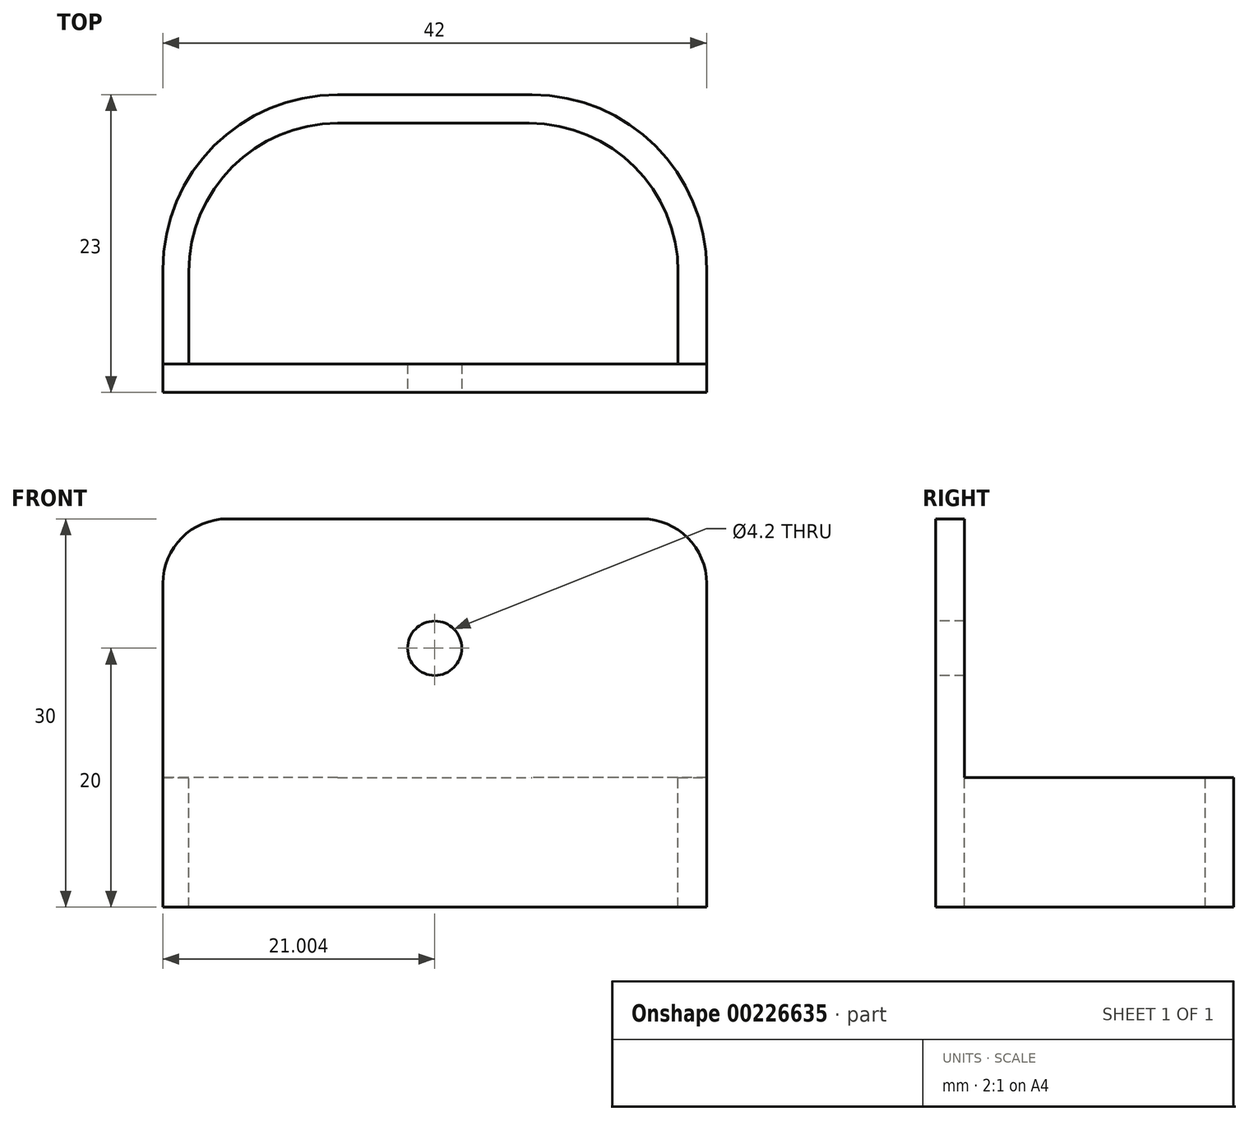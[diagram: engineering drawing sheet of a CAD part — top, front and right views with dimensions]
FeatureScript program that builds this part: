
annotation { "Feature Type Name" : "Feature", "Feature Type Description" : "" }
export const myFeature = defineFeature(function(context is Context, id is Id, definition is map)
    precondition{}
    {
        {
            var Q0;
            Q0=qCreatedBy(makeId("Top.planeOp"),FACE);
            var sketch = newSketch(context, id + "F0", { "sketchPlane" : qUnion([Q0])});
            skLineSegment(sketch, "E0.bottom", {"start": v(36.72, -41.29) * mm, "end": v(51.72, -41.29) * mm});
            skLineSegment(sketch, "E0.top", {"start": v(23.22, -64.29) * mm, "end": v(65.22, -64.29) * mm});
            skLineSegment(sketch, "E0.left", {"start": v(23.22, -54.79) * mm, "end": v(23.22, -64.29) * mm});
            skLineSegment(sketch, "E0.right", {"start": v(65.22, -54.79) * mm, "end": v(65.22, -64.29) * mm});
            skArc(sketch, "E1.filletArc", {"start": v(36.72, -41.29) * mm, "mid": v(27.18, -45.24) * mm, "end": v(23.22, -54.79) * mm});
            skArc(sketch, "E2.filletArc", {"start": v(65.22, -54.79) * mm, "mid": v(61.27, -45.24) * mm, "end": v(51.72, -41.29) * mm});
            skSolve(sketch);
        }
        {
            var Q0;
            Q0=makeQuery(id+"F0.imprint","IMPRINT",FACE,{"disambiguationData":[TD([[makeQuery(id+"F0.imprint","IMPRINT",EDGE,{"derivedFrom":sQuery(id+"F0.wireOp",EDGE,"E0.bottom")}),-1.0]])]});
            extrude(context, id + "F1", {"entities" : qUnion([Q0]), "depth" : 10 * mm});
        }
        {
            var Q0;
            Q0=makeQuery(id+"F1.opExtrude","CAP_FACE",FACE,{"disambiguationData":[OSD([sQuery(id+"F0.wireOp",EDGE,"E0.bottom"),sQuery(id+"F0.wireOp",EDGE,"E0.top"),sQuery(id+"F0.wireOp",EDGE,"E0.left"),sQuery(id+"F0.wireOp",EDGE,"E0.right"),sQuery(id+"F0.wireOp",EDGE,"E1.filletArc"),sQuery(id+"F0.wireOp",EDGE,"E2.filletArc")])],"isStart":false});
            var sketch = newSketch(context, id + "F2", { "sketchPlane" : qUnion([Q0])});
            skLineSegment(sketch, "E3.bottom", {"start": v(36.72, -43.49) * mm, "end": v(51.52, -43.49) * mm});
            skLineSegment(sketch, "E3.top", {"start": v(25.22, -62.09) * mm, "end": v(63.02, -62.09) * mm});
            skLineSegment(sketch, "E3.left", {"start": v(25.22, -54.99) * mm, "end": v(25.22, -62.09) * mm});
            skLineSegment(sketch, "E3.right", {"start": v(63.02, -54.99) * mm, "end": v(63.02, -62.09) * mm});
            skPoint(sketch, "E4.visualSharp", {"position": v(63.02, -43.49) * mm});
            skArc(sketch, "E4.filletArc", {"start": v(63.02, -54.99) * mm, "mid": v(59.66, -46.86) * mm, "end": v(51.52, -43.49) * mm});
            skPoint(sketch, "E5.visualSharp", {"position": v(25.22, -43.49) * mm});
            skArc(sketch, "E5.filletArc", {"start": v(36.72, -43.49) * mm, "mid": v(28.6, -46.86) * mm, "end": v(25.22, -54.99) * mm});
            skSolve(sketch);
        }
        {
            var Q0;
            Q0=qSketchRegion(id+"F2",true);
            extrude(context, id + "F3", {"entities" : qUnion([Q0]), "operationType" : NewBodyOperationType.REMOVE, "oppositeDirection" : true, "depth" : 25 * mm});
        }
        {
            var Q0;
            Q0=makeQuery(id+"F1.opExtrude","CAP_FACE",FACE,{"disambiguationData":[OSD([sQuery(id+"F0.wireOp",EDGE,"E0.bottom"),sQuery(id+"F0.wireOp",EDGE,"E0.top"),sQuery(id+"F0.wireOp",EDGE,"E0.left"),sQuery(id+"F0.wireOp",EDGE,"E0.right"),sQuery(id+"F0.wireOp",EDGE,"E1.filletArc"),sQuery(id+"F0.wireOp",EDGE,"E2.filletArc")])],"isStart":false});
            var sketch = newSketch(context, id + "F4", { "sketchPlane" : qUnion([Q0])});
            skLineSegment(sketch, "E6.bottom", {"start": v(23.22, -64.29) * mm, "end": v(65.22, -64.29) * mm});
            skLineSegment(sketch, "E6.top", {"start": v(23.22, -62.09) * mm, "end": v(65.22, -62.09) * mm});
            skLineSegment(sketch, "E6.left", {"start": v(23.22, -64.29) * mm, "end": v(23.22, -62.09) * mm});
            skLineSegment(sketch, "E6.right", {"start": v(65.22, -64.29) * mm, "end": v(65.22, -62.09) * mm});
            skSolve(sketch);
        }
        {
            var Q0;
            Q0=qSketchRegion(id+"F4",true);
            extrude(context, id + "F5", {"entities" : qUnion([Q0]), "operationType" : NewBodyOperationType.ADD, "depth" : 20 * mm});
        }
        {
            var Q0;
            Q0=makeQuery(id+"F5.boolean.opBoolean","MERGE",FACE,{"derivedFrom":[makeQuery(id+"F1.opExtrude","SWEPT_FACE",FACE,{"disambiguationData":[OSD([sQuery(id+"F0.wireOp",EDGE,"E0.top")])]}),makeQuery(id+"F5.opExtrude","SWEPT_FACE",FACE,{"disambiguationData":[OSD([sQuery(id+"F4.wireOp",EDGE,"E6.bottom")])]})]});
            var sketch = newSketch(context, id + "F6", { "sketchPlane" : qUnion([Q0])});
            skCircle(sketch, "E7", {"center": v(44.22, 20) * mm, "radius": 2.1 * mm});
            skSolve(sketch);
        }
        {
            var Q0;
            Q0=qSketchRegion(id+"F6",true);
            extrude(context, id + "F7", {"entities" : qUnion([Q0]), "operationType" : NewBodyOperationType.REMOVE, "oppositeDirection" : true, "depth" : 4 * mm});
        }
        {
            var Q0;
            Q0=makeQuery(id+"F5.opExtrude","CAP_EDGE",EDGE,{"disambiguationData":[OSD([sQuery(id+"F4.wireOp",EDGE,"E6.right")])],"isStart":false});
            fillet(context, id + "F8", {"entities" : qUnion([Q0]), "radius" : 5 * mm, "tangentPropagation" : true, "allowEdgeOverflow" : false});
        }
        {
            var Q0;
            Q0=makeQuery(id+"F5.opExtrude","CAP_EDGE",EDGE,{"disambiguationData":[OSD([sQuery(id+"F4.wireOp",EDGE,"E6.left")])],"isStart":false});
            fillet(context, id + "F9", {"entities" : qUnion([Q0]), "radius" : 5 * mm, "tangentPropagation" : true, "allowEdgeOverflow" : false});
        }
    });
